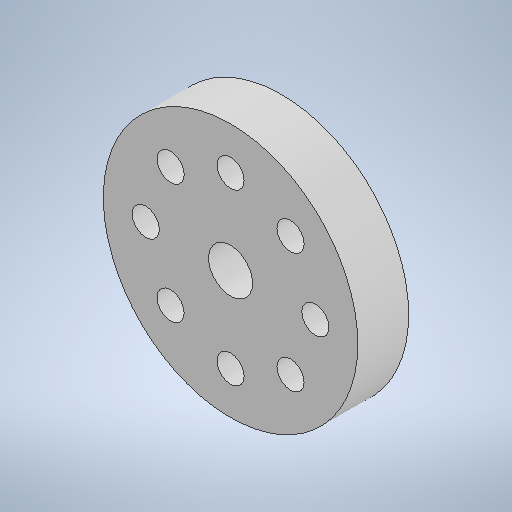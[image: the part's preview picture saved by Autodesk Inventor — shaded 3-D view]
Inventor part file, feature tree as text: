
AUTODESK INVENTOR PART (.ipt)
format: ipt  version: 2025.1 (Build 291241000, 241)  size: 244,736 bytes
history: native  units: mm
features: other x2, extrude x1, sketch x1
ambient origin geometry x8: Origin, YZ Plane, XZ Plane, XY Plane, X Axis, Y Axis, Z Axis, Center Point
bodies: Body1 (feature_tree)
feature tree (4):
  other  "ソリッド1"
  extrude  "押し出し1"  Depth=15.0mm
  sketch  "スケッチ1"
  other  "スケッチ円形状パターン1"
